# Revit family: Drain_Floor_Square-Top_Zurn-Z1727_Medium-duty
name_source: partatom
category: Plumbing Fixtures
units: mm (PartAtom-declared; Revit-internal decimal feet)

## family parameters
Always vertical = Yes
Cut with Voids When Loaded = No
Maintain Annotation Orientation = No
OmniClass Number = 23.45.55.21
OmniClass Title = Drains (Wastes)
Part Type = Normal
Room Calculation Point = No
Round Connector Dimension = Use Radius
Shared = No
Work Plane-Based = No

## types (40) — shared parameters
Assembly Code = D2030300
CW Connection = No
Default Elevation = 20 "
Description = ADJUSTABLE FLOOR DRAIN MEDIUM-DUTY WITH SQUARE TOP
HW Connection = No
Manufacturer = Zurn Water, LLC
Manufacturer Brand = Zurn
Modified Date = 11/14/2025
Product Documentation Link = https://files.zurn.com
Product Page URL = https://www.zurn.com
Product data URL = https://www.bimobject.com
URL = www.zurn.com
Vent Connection = No
Waste Connection = Yes
zero-valued in all types: CWFU, HWFU, WFU

## per-type parameters (varying)
| type | Approx. Weight (Lbs) | Body Height  ' E ' | Grate Open Area (Sq. In.) | Main Material | Model | Pipe Size 'A' (Inner Diameter) | Pipe Size 'A' (Inner Radius) | Pipe Size 'A' (Nominal Diameter) | Pipe Size 'A' (Nominal Radius) | Pipe Size 'A' (Outer Diameter) | Pipe Size 'A' (Outer Radius) | Sq. Dim 'B' | Type Comments |
| Z1727-2BW-5 | 13 " | 2.875 " | 9 m² | Steel - Zurn- Stainless - Type - 304 | Z1727 2BW-5 | 2.067 " | 1.034 " | 2 " | 1 " | 2.375 " | 1.188 " | 5 " | Z1727 2 Inch Butt-Weld Outlet with 5 Inch Square Top. |
| Z1727-2BW-6 | 14 " | 2.875 " | 13 m² | Steel - Zurn- Stainless - Type - 304 | Z1727 2BW-6 | 2.067 " | 1.034 " | 2 " | 1 " | 2.375 " | 1.188 " | 6 " | Z1727 2 Inch Butt-Weld Outlet with 6 Inch Square Top. |
| Z1727-3BW-5 | 13 " | 2.875 " | 9 m² | Steel - Zurn- Stainless - Type - 304 | Z1727 3BW-5 | 3.068 " | 1.534 " | 3 " | 1.5 " | 3.5 " | 1.75 " | 5 " | Z1727 3 Inch Butt-Weld Outlet with 5 Inch Square Top. |
| Z1727-3BW-6 | 14 " | 2.875 " | 13 m² | Steel - Zurn- Stainless - Type - 304 | Z1727 3BW-6 | 3.068 " | 1.534 " | 3 " | 1.5 " | 3.5 " | 1.75 " | 6 " | Z1727 3 Inch Butt-Weld Outlet with 6 Inch Square Top. |
| Z1727-3BW-8 | 18 " | 2.875 " | 25 m² | Steel - Zurn- Stainless - Type - 304 | Z1727 3BW-8 | 3.068 " | 1.534 " | 3 " | 1.5 " | 3.5 " | 1.75 " | 8 " | Z1727 3 Inch Butt-Weld Outlet with 8 Inch Square Top. |
| Z1727-4BW-6 | 14 " | 2.875 " | 13 m² | Steel - Zurn- Stainless - Type - 304 | Z1727 4BW-6 | 4.026 " | 2.013 " | 4 " | 2 " | 4.5 " | 2.25 " | 6 " | Z1727 4 Inch Butt-Weld Outlet with 6 Inch Square Top. |
| Z1727-4BW-8 | 18 " | 2.875 " | 25 m² | Steel - Zurn- Stainless - Type - 304 | Z1727 4BW-8 | 4.026 " | 2.013 " | 4 " | 2 " | 4.5 " | 2.25 " | 8 " | Z1727 4 Inch Butt-Weld Outlet with 8 Inch Square Top. |
| Z1727-6BW-8 | 18 " | 2.875 " | 25 m² | Steel - Zurn- Stainless - Type - 304 | Z1727 6BW-8 | 6.065 " | 3.033 " | 6 " | 3 " | 6.625 " | 3.313 " | 8 " | Z1727 6 Inch Butt-Weld Outlet with 8 Inch Square Top. |
| Z1727-3IC-5 | 13 " | 4.375 " | 9 m² | Steel - Zurn- Stainless - Type - 304 | Z1727 3IC-5 | 3.068 " | 1.534 " | 3 " | 1.5 " | 3.5 " | 1.75 " | 5 " | Z1727 3 Inch Inside Caulk Outlet with 5 Inch Square Top. |
| Z1727-3IC-6 | 14 " | 4.375 " | 13 m² | Steel - Zurn- Stainless - Type - 304 | Z1727 3IC-6 | 3.068 " | 1.534 " | 3 " | 1.5 " | 3.5 " | 1.75 " | 6 " | Z1727 3 Inch Inside Caulk Outlet with 6 Inch Square Top. |
| Z1727-3IC-8 | 18 " | 4.375 " | 25 m² | Steel - Zurn- Stainless - Type - 304 | Z1727 3IC-8 | 3.068 " | 1.534 " | 3 " | 1.5 " | 3.5 " | 1.75 " | 8 " | Z1727 3 Inch Inside Caulk Outlet with 8 Inch Square Top. |
| Z1727-4IC-6 | 14 " | 4.375 " | 13 m² | Steel - Zurn- Stainless - Type - 304 | Z1727 4IC -6 | 4.026 " | 2.013 " | 4 " | 2 " | 4.5 " | 2.25 " | 6 " | Z1727 4 Inch Inside Caulk Outlet  with 6 Inch Square Top. |
| Z1727-4IC-8 | 18 " | 4.375 " | 25 m² | Steel - Zurn- Stainless - Type - 304 | Z1727 4IC -8 | 4.026 " | 2.013 " | 4 " | 2 " | 4.5 " | 2.25 " | 8 " | Z1727 4 Inch Inside Caulk Outlet  with 8 Inch Square Top. |
| Z1727-2IP-5 | 13 " | 2.875 " | 9 m² | Steel - Zurn- Stainless - Type - 304 | Z1727 2IP -5 | 2.067 " | 1.034 " | 2 " | 1 " | 2.375 " | 1.188 " | 5 " | Z1727 2 Inch IP Threaded with 5 Inch Square Top. |
| Z1727-2IP-6 | 14 " | 2.875 " | 13 m² | Steel - Zurn- Stainless - Type - 304 | Z1727 2IP -6 | 2.067 " | 1.034 " | 2 " | 1 " | 2.375 " | 1.188 " | 6 " | Z1727 2 Inch IP Threaded with 6 Inch Square Top. |
| Z1727-3IP-5 | 13 " | 2.875 " | 9 m² | Steel - Zurn- Stainless - Type - 304 | Z1727 3IP -5 | 3.068 " | 1.534 " | 3 " | 1.5 " | 3.5 " | 1.75 " | 5 " | Z1727 3 Inch IP Threaded with 5 Inch Square Top. |
| Z1727-3IP-6 | 14 " | 2.875 " | 13 m² | Steel - Zurn- Stainless - Type - 304 | Z1727 3IP -6 | 3.068 " | 1.534 " | 3 " | 1.5 " | 3.5 " | 1.75 " | 6 " | Z1727 3 Inch IP Threaded with 6 Inch Square Top. |
| Z1727-3IP-8 | 18 " | 2.875 " | 25 m² | Steel - Zurn- Stainless - Type - 304 | Z1727 3IP -8 | 3.068 " | 1.534 " | 3 " | 1.5 " | 3.5 " | 1.75 " | 8 " | Z1727 3 Inch IP Threaded with 8 Inch Square Top. |
| Z1727-4IP-6 | 14 " | 2.875 " | 13 m² | Steel - Zurn- Stainless - Type - 304 | Z1727 4IP -6 | 4.026 " | 2.013 " | 4 " | 2 " | 4.5 " | 2.25 " | 6 " | Z1727 4 Inch IP Threaded with 6 Inch Square Top. |
| Z1727-4IP-8 | 18 " | 2.875 " | 25 m² | Steel - Zurn- Stainless - Type - 304 | Z1727 4IP -8 | 4.026 " | 2.013 " | 4 " | 2 " | 4.5 " | 2.25 " | 8 " | Z1727 4 Inch IP Threaded with 8 Inch Square Top. |
| ZM1727-2BW-5 | 13 " | 2.875 " | 9 m² | Steel - Zurn- Stainless - Type - 316 | ZM1727 2BW-5 | 2.067 " | 1.034 " | 2 " | 1 " | 2.375 " | 1.188 " | 5 " | ZM1727 2 Inch Butt-Weld Outlet with 5 Inch Square Top. |
| ZM1727-2BW-6 | 14 " | 2.875 " | 13 m² | Steel - Zurn- Stainless - Type - 316 | ZM1727 2BW-6 | 2.067 " | 1.034 " | 2 " | 1 " | 2.375 " | 1.188 " | 6 " | ZM1727 2 Inch Butt-Weld Outlet with 6 Inch Square Top. |
| ZM1727-3BW-5 | 13 " | 2.875 " | 9 m² | Steel - Zurn- Stainless - Type - 316 | ZM1727 3BW-5 | 3.068 " | 1.534 " | 3 " | 1.5 " | 3.5 " | 1.75 " | 5 " | ZM1727 3 Inch Butt-Weld Outlet with 5 Inch Square Top. |
| ZM1727-3BW-6 | 14 " | 2.875 " | 13 m² | Steel - Zurn- Stainless - Type - 316 | ZM1727 3BW-6 | 3.068 " | 1.534 " | 3 " | 1.5 " | 3.5 " | 1.75 " | 6 " | ZM1727 3 Inch Butt-Weld Outlet with 6 Inch Square Top. |
| ZM1727-3BW-8 | 18 " | 2.875 " | 25 m² | Steel - Zurn- Stainless - Type - 316 | ZM1727 3BW-8 | 3.068 " | 1.534 " | 3 " | 1.5 " | 3.5 " | 1.75 " | 8 " | ZM1727 3 Inch Butt-Weld Outlet with 8 Inch Square Top. |
| ZM1727-4BW-6 | 14 " | 2.875 " | 13 m² | Steel - Zurn- Stainless - Type - 316 | ZM1727 4BW-6 | 4.026 " | 2.013 " | 4 " | 2 " | 4.5 " | 2.25 " | 6 " | ZM1727 4 Inch Butt-Weld Outlet with 6 Inch Square Top. |
| ZM1727-4BW-8 | 18 " | 2.875 " | 25 m² | Steel - Zurn- Stainless - Type - 316 | ZM1727 4BW-8 | 4.026 " | 2.013 " | 4 " | 2 " | 4.5 " | 2.25 " | 8 " | ZM1727 4 Inch Butt-Weld Outlet with 8 Inch Square Top. |
| ZM1727-6BW-8 | 18 " | 2.875 " | 25 m² | Steel - Zurn- Stainless - Type - 316 | ZM1727 6BW-8 | 6.065 " | 3.033 " | 6 " | 3 " | 6.625 " | 3.313 " | 8 " | ZM1727 6 Inch Butt-Weld Outlet with 8 Inch Square Top. |
| ZM1727-3IC-5 | 13 " | 4.375 " | 9 m² | Steel - Zurn- Stainless - Type - 316 | ZM1727 3IC-5 | 3.068 " | 1.534 " | 3 " | 1.5 " | 3.5 " | 1.75 " | 5 " | ZM1727 3 Inch Inside Caulk Outlet with 5 Inch Square Top. |
| ZM1727-3IC-6 | 14 " | 4.375 " | 13 m² | Steel - Zurn- Stainless - Type - 316 | ZM1727 3IC-6 | 3.068 " | 1.534 " | 3 " | 1.5 " | 3.5 " | 1.75 " | 6 " | ZM1727 3 Inch Inside Caulk Outlet with 6 Inch Square Top. |
| ZM1727-3IC-8 | 18 " | 4.375 " | 25 m² | Steel - Zurn- Stainless - Type - 316 | ZM1727 3IC-8 | 3.068 " | 1.534 " | 3 " | 1.5 " | 3.5 " | 1.75 " | 8 " | ZM1727 3 Inch Inside Caulk Outlet with 8 Inch Square Top. |
| ZM1727-4IC-6 | 14 " | 4.375 " | 13 m² | Steel - Zurn- Stainless - Type - 316 | ZM1727 4IC -6 | 4.026 " | 2.013 " | 4 " | 2 " | 4.5 " | 2.25 " | 6 " | ZM1727 4 Inch Inside Caulk Outlet  with 6 Inch Square Top. |
| ZM1727-4IC-8 | 18 " | 4.375 " | 25 m² | Steel - Zurn- Stainless - Type - 316 | ZM1727 4IC -8 | 4.026 " | 2.013 " | 4 " | 2 " | 4.5 " | 2.25 " | 8 " | ZM1727 4 Inch Inside Caulk Outlet  with 8 Inch Square Top. |
| ZM1727-2IP-5 | 13 " | 2.875 " | 9 m² | Steel - Zurn- Stainless - Type - 316 | ZM1727 2IP -5 | 2.067 " | 1.034 " | 2 " | 1 " | 2.375 " | 1.188 " | 5 " | ZM1727 2 Inch IP Threaded with 5 Inch Square Top. |
| ZM1727-2IP-6 | 14 " | 2.875 " | 13 m² | Steel - Zurn- Stainless - Type - 316 | ZM1727 2IP -6 | 2.067 " | 1.034 " | 2 " | 1 " | 2.375 " | 1.188 " | 6 " | ZM1727 2 Inch IP Threaded with 6 Inch Square Top. |
| ZM1727-3IP-5 | 13 " | 2.875 " | 9 m² | Steel - Zurn- Stainless - Type - 316 | ZM1727 3IP -5 | 3.068 " | 1.534 " | 3 " | 1.5 " | 3.5 " | 1.75 " | 5 " | ZM1727 3 Inch IP Threaded with 5 Inch Square Top. |
| ZM1727-3IP-6 | 14 " | 2.875 " | 13 m² | Steel - Zurn- Stainless - Type - 316 | ZM1727 3IP -6 | 3.068 " | 1.534 " | 3 " | 1.5 " | 3.5 " | 1.75 " | 6 " | ZM1727 3 Inch IP Threaded with 6 Inch Square Top. |
| ZM1727-3IP-8 | 18 " | 2.875 " | 25 m² | Steel - Zurn- Stainless - Type - 316 | ZM1727 3IP -8 | 3.068 " | 1.534 " | 3 " | 1.5 " | 3.5 " | 1.75 " | 8 " | ZM1727 3 Inch IP Threaded with 8 Inch Square Top. |
| ZM1727-4IP-6 | 14 " | 2.875 " | 13 m² | Steel - Zurn- Stainless - Type - 316 | ZM1727 4IP -6 | 4.026 " | 2.013 " | 4 " | 2 " | 4.5 " | 2.25 " | 6 " | ZM1727 4 Inch IP Threaded with 6 Inch Square Top. |
| ZM1727-4IP-8 | 18 " | 2.875 " | 25 m² | Steel - Zurn- Stainless - Type - 316 | ZM1727 4IP -8 | 4.026 " | 2.013 " | 4 " | 2 " | 4.5 " | 2.25 " | 8 " | ZM1727 4 Inch IP Threaded with 8 Inch Square Top. |

## geometry (parser evidence)
native form markers: Sweep x2
no freeform markers — native parametric forms only
